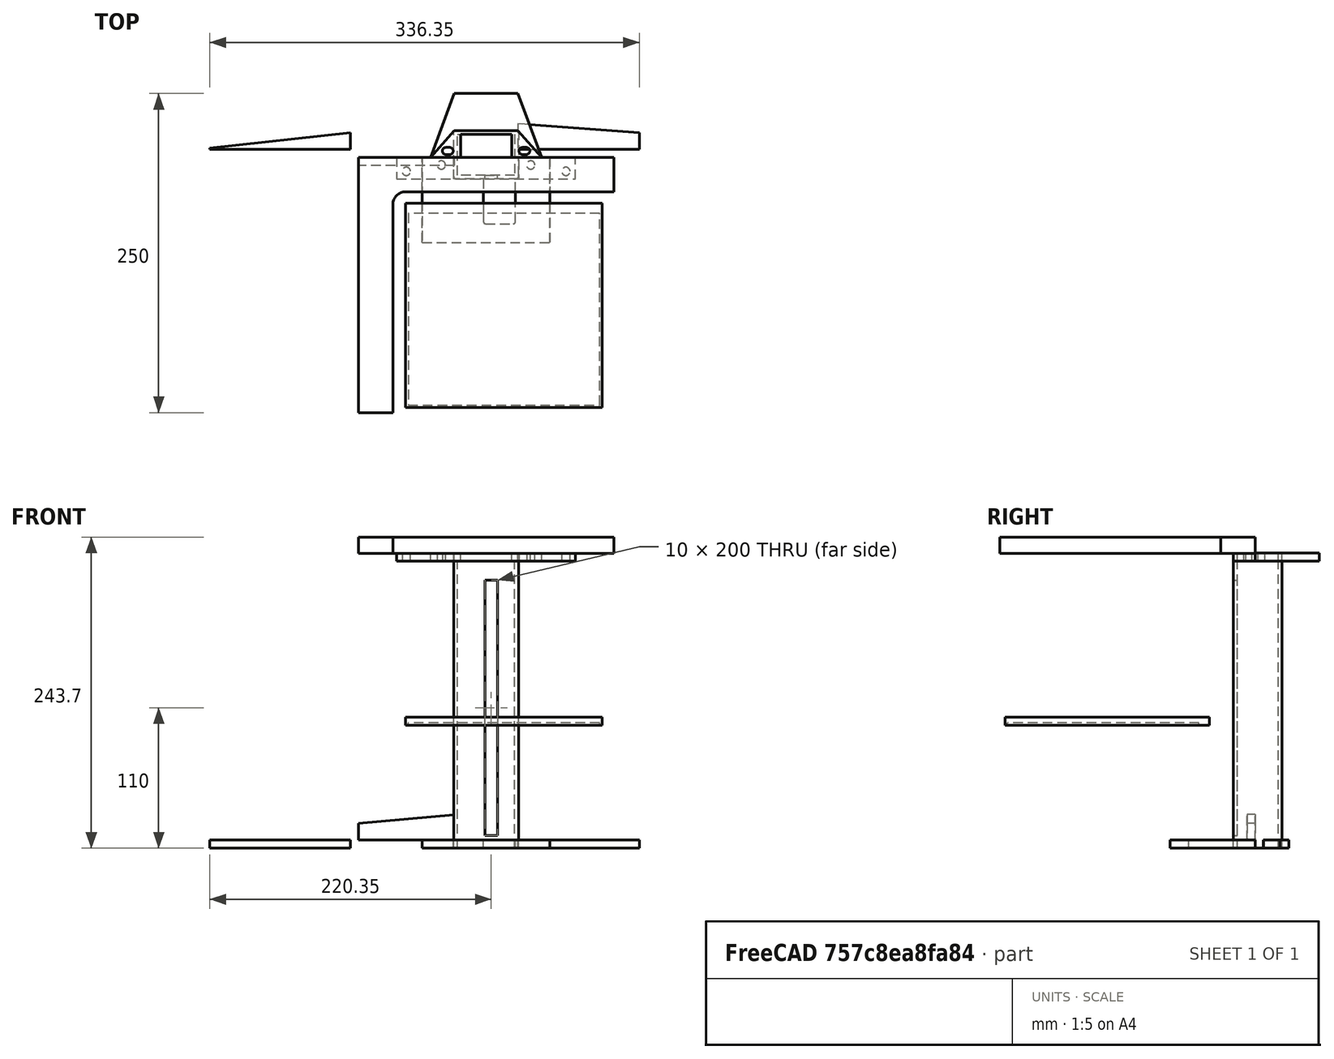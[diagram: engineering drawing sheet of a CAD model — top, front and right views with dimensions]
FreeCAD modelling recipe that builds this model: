
FCSTD DOCUMENT  (FreeCAD 0.19R)
Label: Printer3_tbp
License: All rights reserved
LicenseURL: http://en.wikipedia.org/wiki/All_rights_reserved
objects: Sketcher::SketchObject×18, PartDesign::Pad×9, PartDesign::Body×9, PartDesign::Pocket×4, PartDesign::Fillet×1, Mesh::Feature×1
note: 55 computed .brp shape members not serialized (recipe doc carries the construction recipe); baked Part::Feature solids carry a one-line shape summary decoded from their .brp

FEATURE [Sketcher::SketchObject] Sketch
  FullyConstrained = false
  MapMode = 5
  sketch-geometry (25):
    g0: LineSegment StartX=220 StartY=-2.5 StartZ=0 EndX=220 EndY=-219.878 EndZ=0
    g1: LineSegment StartX=210 StartY=-229.878 StartZ=0 EndX=10 EndY=-229.878 EndZ=0
    g2: LineSegment StartX=0 StartY=-219.878 StartZ=0 EndX=0 EndY=-2.5 EndZ=0
    g3: LineSegment StartX=2.5 StartY=0 StartZ=0 EndX=74.5 EndY=0 EndZ=0
    g4: LineSegment StartX=74.5 StartY=0 StartZ=0 EndX=74.5 EndY=-14.5 EndZ=0
    g5: LineSegment StartX=125.5 StartY=-14.5 StartZ=0 EndX=125.5 EndY=0 EndZ=0
    g6: LineSegment StartX=125.5 StartY=0 StartZ=0 EndX=217.5 EndY=0 EndZ=0
    g7: LineSegment StartX=100 StartY=29.7116 StartZ=0 EndX=100 EndY=-38.9559 EndZ=0
    g8: ArcOfCircle CenterX=2.5 CenterY=-2.5 CenterZ=0 NormalX=0 NormalY=0 NormalZ=1 AngleXU=0 Radius=2.5 StartAngle=1.5708 EndAngle=3.14159
    g9: ArcOfCircle CenterX=217.5 CenterY=-2.5 CenterZ=0 NormalX=0 NormalY=0 NormalZ=1 AngleXU=0 Radius=2.5 StartAngle=4.63e-14 EndAngle=1.5708
    g10: ArcOfCircle CenterX=210 CenterY=-219.878 CenterZ=0 NormalX=0 NormalY=0 NormalZ=1 AngleXU=0 Radius=10 StartAngle=4.71239 EndAngle=6.28319
    g11: ArcOfCircle CenterX=10 CenterY=-219.878 CenterZ=0 NormalX=0 NormalY=0 NormalZ=1 AngleXU=0 Radius=10 StartAngle=3.14159 EndAngle=4.71239
    g12: ArcOfCircle CenterX=123 CenterY=-14.5 CenterZ=0 NormalX=0 NormalY=0 NormalZ=1 AngleXU=0 Radius=2.5 StartAngle=4.71239 EndAngle=6.28319
    g13: ArcOfCircle CenterX=77 CenterY=-14.5 CenterZ=0 NormalX=0 NormalY=0 NormalZ=1 AngleXU=0 Radius=2.5 StartAngle=3.14159 EndAngle=4.71239
    g14: LineSegment StartX=98 StartY=-17 StartZ=0 EndX=98 EndY=-50.5 EndZ=0
    g15: LineSegment StartX=99.5 StartY=-52 StartZ=0 EndX=121.5 EndY=-52 EndZ=0
    g16: LineSegment StartX=123 StartY=-50.5 StartZ=0 EndX=123 EndY=-17 EndZ=0
    g17: LineSegment StartX=77 StartY=-17 StartZ=0 EndX=98 EndY=-17 EndZ=0
    g18: ArcOfCircle CenterX=99.5 CenterY=-50.5 CenterZ=0 NormalX=0 NormalY=0 NormalZ=1 AngleXU=0 Radius=1.5 StartAngle=3.14159 EndAngle=4.71239
    g19: ArcOfCircle CenterX=121.5 CenterY=-50.5 CenterZ=0 NormalX=0 NormalY=0 NormalZ=1 AngleXU=0 Radius=1.5 StartAngle=4.71239 EndAngle=6.28319
    g20: Circle CenterX=207 CenterY=-216.878 CenterZ=0 NormalX=0 NormalY=0 NormalZ=1 AngleXU=0 Radius=2.25
    g21: Circle CenterX=13 CenterY=-216.878 CenterZ=0 NormalX=0 NormalY=0 NormalZ=1 AngleXU=0 Radius=2.25
    g22: Circle CenterX=207 CenterY=-13 CenterZ=0 NormalX=0 NormalY=0 NormalZ=1 AngleXU=0 Radius=2.25
    g23: Circle CenterX=13 CenterY=-13 CenterZ=0 NormalX=0 NormalY=0 NormalZ=1 AngleXU=0 Radius=2.25
    g24: LineSegment StartX=110 StartY=54.384 StartZ=0 EndX=110 EndY=-317.389 EndZ=0
  constraints (63):
    c: Vertical(g0)
    c: Vertical(g2)
    c: Equal(g2,g0)
    c: PointOnObject(g3,g-1)
    c: Horizontal(g3)
    c: Coincident(g3,g4)
    c: PointOnObject(g5,g-1)
    c: Coincident(g5,g6)
    c: Horizontal(g6)
    c: Vertical(g5)
    c: Vertical(g4)
    c: Symmetric(g5,g3,g7)
    c: DistanceX(g7) = 100
    c: Tangent(g2,g8) = 1.5708
    c: Tangent(g3,g8) = 1.5708
    c: Tangent(g6,g9) = 1.5708
    c: Tangent(g0,g9) = 1.5708
    c: Tangent(g1,g10) = 1.5708
    c: Tangent(g0,g10) = 1.5708
    c: Tangent(g1,g11) = 1.5708
    c: Tangent(g2,g11) = 1.5708
    c: PointOnObject(g2,g-2)
    c: Tangent(g5,g12) = -1.5708
    c: Tangent(g4,g13) = -1.5708
    c: Equal(g12,g13)
    c: Distance(g5,g3) = 51
    c: Vertical(g14)
    c: Vertical(g16)
    c: Horizontal(g17)
    c: DistanceY(g12) = -17
    c: Tangent(g14,g18) = -1.5708
    c: Tangent(g15,g18) = -1.5708
    c: Tangent(g16,g19) = -1.5708
    c: Tangent(g15,g19) = -1.5708
    c: DistanceY(g17) = -17
    c: Distance(g16,g14) = 25
    c: Tangent(g17,g13) = -1.5708
    c: DistanceY(g15,g16) = 35
    c: Coincident(g14,g17)
    c: Horizontal(g15)
    c: Diameter(g19) = 3
    c: Diameter(g10) = 20
    c: Diameter(g11) = 20
    c: Diameter(g9) = 5
    c: Diameter(g8) = 5
    c: Distance(g0,g2) = 220
    c: Distance(g6,g1) = 230
    c: Diameter(g18) = 3
    c: Diameter(g13) = 5
    c: Coincident(g16,g12)
    c: Perpendicular(g12,g16)
    c: Diameter(g23) = 4.5
    c: Equal(g23,g22)
    c: Equal(g23,g20)
    c: Diameter(g21) = 4.5
    c: Vertical(g24)
    c: DistanceX(g24) = 110
    c: Symmetric(g22,g23,g24)
    c: Symmetric(g20,g21,g24)
    c: Distance(g20,g0) = 13
    c: Distance(g20,g1) = 13
    c: Distance(g22,g0) = 13
    c: Distance(g22,g6) = 13
FEATURE [PartDesign::Pad] Pad
  Direction = (1,1,1)
  Length = 6.35
  Length2 = 100
  Profile = -> Sketch
  Type = 0
FEATURE [Sketcher::SketchObject] Sketch006
  FullyConstrained = false
  MapMode = 5
  Support = -> [XY_Plane002]
  sketch-geometry (9):
    g0: LineSegment StartX=74.6 StartY=21 StartZ=0 EndX=125.4 EndY=21 EndZ=0
    g1: LineSegment StartX=125.4 StartY=21 StartZ=0 EndX=125.4 EndY=-17 EndZ=0
    g2: LineSegment StartX=125.4 StartY=-17 StartZ=0 EndX=74.6 EndY=-17 EndZ=0
    g3: LineSegment StartX=74.6 StartY=-17 StartZ=0 EndX=74.6 EndY=21 EndZ=0
    g4: LineSegment StartX=100 StartY=34.7898 StartZ=0 EndX=100 EndY=11.1526 EndZ=0
    g5: LineSegment StartX=77.6 StartY=18 StartZ=0 EndX=122.4 EndY=18 EndZ=0
    g6: LineSegment StartX=122.4 StartY=18 StartZ=0 EndX=122.4 EndY=-14 EndZ=0
    g7: LineSegment StartX=122.4 StartY=-14 StartZ=0 EndX=77.6 EndY=-14 EndZ=0
    g8: LineSegment StartX=77.6 StartY=-14 StartZ=0 EndX=77.6 EndY=18 EndZ=0
  constraints (25):
    c: Coincident(g0,g1)
    c: Coincident(g1,g2)
    c: Coincident(g2,g3)
    c: Coincident(g3,g0)
    c: Horizontal(g0)
    c: Horizontal(g2)
    c: Vertical(g1)
    c: Vertical(g3)
    c: Distance(g0) = 50.8
    c: Distance(g1) = 38
    c: DistanceY(g1,g-1) = 17
    c: Symmetric(g0,g0,g4)
    c: DistanceX(g4) = 100
    c: Coincident(g5,g6)
    c: Coincident(g6,g7)
    c: Coincident(g7,g8)
    c: Coincident(g8,g5)
    c: Horizontal(g5)
    c: Horizontal(g7)
    c: Vertical(g6)
    c: Vertical(g8)
    c: Distance(g5,g1) = 3
    c: Distance(g5,g0) = 3
    c: Distance(g7,g3) = 3
    c: Distance(g6,g2) = 3
FEATURE [PartDesign::Pad] Pad001
  Direction = (1,1,1)
  Length = 225
  Length2 = 100
  Profile = -> Sketch006
  Type = 0
FEATURE [Sketcher::SketchObject] Sketch007
  FullyConstrained = true
  MapMode = 5
  Placement = pos=(0,-17,0) rot=(1,0,0;1.5708rad)
  Support = -> [Pad001]
  sketch-geometry (4):
    g0: LineSegment StartX=99 StartY=210 StartZ=0 EndX=109 EndY=210 EndZ=0
    g1: LineSegment StartX=109 StartY=210 StartZ=0 EndX=109 EndY=10 EndZ=0
    g2: LineSegment StartX=109 StartY=10 StartZ=0 EndX=99 EndY=10 EndZ=0
    g3: LineSegment StartX=99 StartY=10 StartZ=0 EndX=99 EndY=210 EndZ=0
  constraints (12):
    c: Coincident(g0,g1)
    c: Coincident(g1,g2)
    c: Coincident(g2,g3)
    c: Coincident(g3,g0)
    c: Horizontal(g0)
    c: Horizontal(g2)
    c: Vertical(g1)
    c: Vertical(g3)
    c: Distance(g2) = 10
    c: DistanceX(g1) = 109
    c: DistanceY(g1) = 10
    c: Distance(g1) = 200
FEATURE [PartDesign::Pocket] Pocket
  BaseFeature = -> Pad001
  Length = 5
  Length2 = 100
  Profile = -> Sketch007
  Type = 0
FEATURE [Sketcher::SketchObject] Sketch009
  FullyConstrained = true
  MapMode = 5
  Placement = pos=(0,0,0) rot=(1,0,0;1.5708rad)
  Support = -> [XZ_Plane004]
  sketch-geometry (4):
    g0: LineSegment StartX=75 StartY=6.35 StartZ=0 EndX=75 EndY=26.35 EndZ=0
    g1: LineSegment StartX=75 StartY=26.35 StartZ=0 EndX=0 EndY=19.35 EndZ=0
    g2: LineSegment StartX=0 StartY=19.35 StartZ=0 EndX=0 EndY=6.35 EndZ=0
    g3: LineSegment StartX=0 StartY=6.35 StartZ=0 EndX=75 EndY=6.35 EndZ=0
  constraints (12):
    c: Vertical(g0)
    c: Coincident(g0,g1)
    c: Coincident(g1,g2)
    c: Coincident(g2,g3)
    c: Coincident(g3,g0)
    c: Horizontal(g3)
    c: Distance(g0) = 20
    c: Vertical(g2)
    c: Distance(g2) = 13
    c: DistanceX(g0) = 75
    c: DistanceY(g2) = 6.35
    c: PointOnObject(g1,g-2)
FEATURE [PartDesign::Pad] Pad003
  Direction = (1,1,1)
  Length = 6.35
  Length2 = 100
  Placement = pos=(0,0,0) rot=(1,0,0;1.5708rad)
  Profile = -> Sketch009
  Type = 0
FEATURE [PartDesign::Body] Body004  label="Gusset1"
  Group = -> [Sketch009,Pad003]
  Origin = -> Origin004
  Placement = pos=(0,-22,0) rot=(0,0,1;0rad)
  Tip = -> Pad003
FEATURE [Sketcher::SketchObject] Sketch010
  FullyConstrained = true
  MapMode = 5
  sketch-geometry (4):
    g0: LineSegment StartX=-6.35 StartY=6.35 StartZ=0 EndX=-6.35 EndY=19.35 EndZ=0
    g1: LineSegment StartX=-6.35 StartY=19.35 StartZ=0 EndX=-116.35 EndY=7.35 EndZ=0
    g2: LineSegment StartX=-116.35 StartY=7.35 StartZ=0 EndX=-116.35 EndY=6.35 EndZ=0
    g3: LineSegment StartX=-116.35 StartY=6.35 StartZ=0 EndX=-6.35 EndY=6.35 EndZ=0
  constraints (12):
    c: Vertical(g0)
    c: Coincident(g0,g1)
    c: Coincident(g1,g2)
    c: Vertical(g2)
    c: Coincident(g2,g3)
    c: Coincident(g3,g0)
    c: Horizontal(g3)
    c: Distance(g2) = 1
    c: Distance(g0) = 13
    c: DistanceY(g0) = 6.35
    c: DistanceX(g0) = -6.35
    c: Distance(g3) = 110
FEATURE [PartDesign::Pad] Pad004
  Direction = (1,1,1)
  Length = 6.35
  Length2 = 100
  Profile = -> Sketch010
  Type = 0
FEATURE [PartDesign::Body] Body005  label="Gusset2"
  Group = -> [Sketch010,Pad004]
  Origin = -> Origin005
  Placement = pos=(0,-22,0) rot=(0,0,1;0rad)
  Tip = -> Pad004
FEATURE [Sketcher::SketchObject] Sketch011
  FullyConstrained = true
  MapMode = 5
  sketch-geometry (4):
    g0: LineSegment StartX=125 StartY=26.35 StartZ=0 EndX=125 EndY=6.35 EndZ=0
    g1: LineSegment StartX=125 StartY=6.35 StartZ=0 EndX=220 EndY=6.35 EndZ=0
    g2: LineSegment StartX=220 StartY=6.35 StartZ=0 EndX=220 EndY=19.35 EndZ=0
    g3: LineSegment StartX=220 StartY=19.35 StartZ=0 EndX=125 EndY=26.35 EndZ=0
  constraints (12):
    c: Vertical(g0)
    c: Coincident(g0,g1)
    c: Horizontal(g1)
    c: Coincident(g1,g2)
    c: Vertical(g2)
    c: Coincident(g2,g3)
    c: Coincident(g3,g0)
    c: Distance(g0) = 20
    c: DistanceY(g0) = 6.35
    c: DistanceX(g0) = 125
    c: DistanceX(g2) = 220
    c: Distance(g2) = 13
FEATURE [PartDesign::Pad] Pad005
  Direction = (1,1,1)
  Length = 6.35
  Length2 = 100
  Profile = -> Sketch011
  Type = 0
FEATURE [PartDesign::Body] Body006  label="Gusset3"
  Group = -> [Sketch011,Pad005]
  Origin = -> Origin006
  Placement = pos=(0,-22,0) rot=(0,0,1;0rad)
  Tip = -> Pad005
FEATURE [Sketcher::SketchObject] Sketch012
  FullyConstrained = false
  MapMode = 5
  Support = -> [XY_Plane007]
  sketch-geometry (5):
    g0: LineSegment StartX=37 StartY=-30 StartZ=0 EndX=191 EndY=-30 EndZ=0
    g1: LineSegment StartX=191 StartY=-30 StartZ=0 EndX=191 EndY=-190 EndZ=0
    g2: LineSegment StartX=191 StartY=-190 StartZ=0 EndX=37 EndY=-190 EndZ=0
    g3: LineSegment StartX=37 StartY=-190 StartZ=0 EndX=37 EndY=-30 EndZ=0
    g4: LineSegment StartX=114 StartY=-22.3792 StartZ=0 EndX=114 EndY=-218.376 EndZ=0
  constraints (13):
    c: Coincident(g0,g1)
    c: Coincident(g1,g2)
    c: Coincident(g2,g3)
    c: Coincident(g3,g0)
    c: Horizontal(g0)
    c: Horizontal(g2)
    c: Vertical(g1)
    c: Vertical(g3)
    c: DistanceX(g0) = 37
    c: DistanceY(g0) = -30
    c: Distance(g2) = 154
    c: Distance(g1) = 160
    c: Symmetric(g0,g0,g4)
FEATURE [PartDesign::Pad] Pad006
  Direction = (1,1,1)
  Length = 6.35
  Length2 = 100
  Profile = -> Sketch012
  Type = 0
FEATURE [Sketcher::SketchObject] Sketch013
  FullyConstrained = true
  MapMode = 5
  Placement = pos=(0,0,0) rot=(1,0,0;3.14159rad)
  Support = -> [Pad006]
  sketch-geometry (4):
    g0: LineSegment StartX=39 StartY=188 StartZ=0 EndX=189 EndY=188 EndZ=0
    g1: LineSegment StartX=189 StartY=188 StartZ=0 EndX=189 EndY=38 EndZ=0
    g2: LineSegment StartX=189 StartY=38 StartZ=0 EndX=39 EndY=38 EndZ=0
    g3: LineSegment StartX=39 StartY=38 StartZ=0 EndX=39 EndY=188 EndZ=0
  constraints (12):
    c: Coincident(g0,g1)
    c: Coincident(g1,g2)
    c: Coincident(g2,g3)
    c: Coincident(g3,g0)
    c: Horizontal(g0)
    c: Horizontal(g2)
    c: Vertical(g1)
    c: Vertical(g3)
    c: Distance(g0) = 150
    c: DistanceY(g0) = 188
    c: Distance(g1) = 150
    c: DistanceX(g0) = 39
FEATURE [PartDesign::Pocket] Pocket001
  BaseFeature = -> Pad006
  Length = 2
  Length2 = 100
  Profile = -> Sketch013
  Type = 0
FEATURE [PartDesign::Body] Body007  label="Bed"
  Group = -> [Sketch012,Pad006,Sketch013,Pocket001]
  Origin = -> Origin007
  Placement = pos=(0,-28,96.35) rot=(0,0,1;0rad)
  Tip = -> Pocket001
FEATURE [Sketcher::SketchObject] Sketch014
  FullyConstrained = true
  MapMode = 5
  Support = -> [XY_Plane008]
  sketch-geometry (4):
    g0: LineSegment StartX=0 StartY=0 StartZ=0 EndX=200 EndY=0 EndZ=0
    g1: LineSegment StartX=200 StartY=0 StartZ=0 EndX=200 EndY=-200 EndZ=0
    g2: LineSegment StartX=200 StartY=-200 StartZ=0 EndX=0 EndY=-200 EndZ=0
    g3: LineSegment StartX=0 StartY=-200 StartZ=0 EndX=0 EndY=0 EndZ=0
  constraints (11):
    c: Coincident(g0,g1)
    c: Coincident(g1,g2)
    c: Coincident(g2,g3)
    c: Coincident(g3,g0)
    c: Horizontal(g0)
    c: Horizontal(g2)
    c: Vertical(g1)
    c: Vertical(g3)
    c: Coincident(g0,g-1)
    c: Distance(g0) = 200
    c: Distance(g1) = 200
FEATURE [PartDesign::Pad] Pad007
  Direction = (1,1,1)
  Length = 12.7
  Length2 = 100
  Profile = -> Sketch014
  Type = 0
FEATURE [Sketcher::SketchObject] Sketch015
  FullyConstrained = false
  MapMode = 5
  Placement = pos=(0,0,12.7) rot=(0,0,1;0rad)
  Support = -> [Pad007]
  sketch-geometry (4):
    g0: LineSegment StartX=27 StartY=-27 StartZ=0 EndX=356.815 EndY=-27 EndZ=0
    g1: LineSegment StartX=356.815 StartY=-27 StartZ=0 EndX=356.815 EndY=-319.156 EndZ=0
    g2: LineSegment StartX=356.815 StartY=-319.156 StartZ=0 EndX=27 EndY=-319.156 EndZ=0
    g3: LineSegment StartX=27 StartY=-319.156 StartZ=0 EndX=27 EndY=-27 EndZ=0
  constraints (10):
    c: Coincident(g0,g1)
    c: Coincident(g1,g2)
    c: Coincident(g2,g3)
    c: Coincident(g3,g0)
    c: Horizontal(g0)
    c: Horizontal(g2)
    c: Vertical(g1)
    c: Vertical(g3)
    c: DistanceX(g0) = 27
    c: DistanceY(g0) = -27
FEATURE [PartDesign::Pocket] Pocket002
  BaseFeature = -> Pad007
  Length = 13
  Length2 = 100
  Profile = -> Sketch015
  Type = 0
FEATURE [PartDesign::Fillet] Fillet
  Base = -> Pocket002 [Edge18]
  BaseFeature = -> Pocket002
  Radius = 10
  SupportTransform = false
FEATURE [Sketcher::SketchObject] Sketch016
  FullyConstrained = false
  MapMode = 5
  Placement = pos=(0,0,0) rot=(1,0,0;3.14159rad)
  Support = -> [Pad]
  sketch-geometry (8):
    g0: LineSegment StartX=150 StartY=11.5558 StartZ=0 EndX=150 EndY=-66.6529 EndZ=0
    g1: LineSegment StartX=150 StartY=-66.6529 StartZ=0 EndX=50 EndY=-66.6529 EndZ=0
    g2: LineSegment StartX=50 StartY=-66.6529 StartZ=0 EndX=50 EndY=26.8046 EndZ=0
    g3: LineSegment StartX=50 StartY=26.8046 StartZ=0 EndX=-42.6332 EndY=26.8046 EndZ=0
    g4: LineSegment StartX=-42.6332 StartY=26.8046 StartZ=0 EndX=-42.6332 EndY=-265.193 EndZ=0
    g5: LineSegment StartX=-42.6332 StartY=-265.193 StartZ=0 EndX=358.07 EndY=-265.193 EndZ=0
    g6: LineSegment StartX=358.07 StartY=-265.193 StartZ=0 EndX=358.07 EndY=30.5784 EndZ=0
    g7: LineSegment StartX=358.07 StartY=30.5784 StartZ=0 EndX=150 EndY=11.5558 EndZ=0
  constraints (17):
    c: Vertical(g0)
    c: Coincident(g0,g1)
    c: Horizontal(g1)
    c: Coincident(g1,g2)
    c: Vertical(g2)
    c: Coincident(g2,g3)
    c: Horizontal(g3)
    c: Coincident(g3,g4)
    c: Vertical(g4)
    c: Coincident(g4,g5)
    c: Horizontal(g5)
    c: Coincident(g5,g6)
    c: Vertical(g6)
    c: Coincident(g6,g7)
    c: Coincident(g7,g0)
    c: DistanceX(g1) = 50
    c: DistanceX(g0) = 150
FEATURE [PartDesign::Pocket] Pocket003
  BaseFeature = -> Pad
  Length = 9
  Length2 = 100
  Profile = -> Sketch016
  Type = 0
FEATURE [Sketcher::SketchObject] Sketch017
  FullyConstrained = false
  MapMode = 5
  Placement = pos=(0,-17,0) rot=(1,0,0;1.5708rad)
  Support = -> [Pocket]
  sketch-geometry (9):
    g0: LineSegment StartX=89 StartY=196.442 StartZ=0 EndX=97 EndY=196.442 EndZ=0
    g1: LineSegment StartX=97 StartY=196.442 StartZ=0 EndX=97 EndY=176.538 EndZ=0
    g2: LineSegment StartX=97 StartY=176.538 StartZ=0 EndX=89 EndY=176.538 EndZ=0
    g3: LineSegment StartX=89 StartY=176.538 StartZ=0 EndX=89 EndY=196.442 EndZ=0
    g4: LineSegment StartX=100 StartY=275.798 StartZ=0 EndX=100 EndY=-189.424 EndZ=0
    g5: LineSegment StartX=93 StartY=214.672 StartZ=0 EndX=93 EndY=194.243 EndZ=0
    g6: LineSegment StartX=123 StartY=219.526 StartZ=0 EndX=123 EndY=197.969 EndZ=0
    g7: LineSegment StartX=102.65 StartY=201.069 StartZ=0 EndX=102.65 EndY=188.207 EndZ=0
    g8: LineSegment StartX=109 StartY=200.806 StartZ=0 EndX=109 EndY=186.098 EndZ=0
  constraints (19):
    c: Coincident(g0,g1)
    c: Coincident(g1,g2)
    c: Coincident(g2,g3)
    c: Coincident(g3,g0)
    c: Horizontal(g0)
    c: Horizontal(g2)
    c: Vertical(g1)
    c: Vertical(g3)
    c: Vertical(g4)
    c: DistanceX(g4) = 100
    c: Distance(g0) = 8
    c: Vertical(g6)
    c: Distance(g6,g4) = 23
    c: Distance(g5,g6) = 30
    c: Symmetric(g0,g0,g5)
    c: Vertical(g7)
    c: Distance(g7,g6) = 20.35
    c: Vertical(g8)
    c: Distance(g8,g7) = 6.35
FEATURE [Sketcher::SketchObject] Sketch018
  FullyConstrained = true
  MapMode = 5
  Placement = pos=(0,0,225) rot=(0,0,1;0rad)
  Support = -> [Pocket]
FEATURE [PartDesign::Body] Body002  label="Column"
  Group = -> [Sketch006,Pad001,Sketch007,Pocket,Sketch017,Sketch018]
  Origin = -> Origin002
  Placement = pos=(0,-22,0) rot=(0,0,1;0rad)
  Tip = -> Pocket
FEATURE [Sketcher::SketchObject] Sketch019
  ExternalGeometry = -> [Pocket003]
  FullyConstrained = true
  MapMode = 5
  Placement = pos=(0,0,6.35) rot=(0,0,1;0rad)
  Support = -> [Pocket003]
FEATURE [Sketcher::SketchObject] Sketch020
  ExternalGeometry = -> [Pad]
  FullyConstrained = false
  MapMode = 5
  Placement = pos=(0,0,0) rot=(1,0,0;3.14159rad)
  Support = -> [Pad]
  sketch-geometry (4):
    g0: LineSegment StartX=92.1821 StartY=-18.4998 StartZ=0 EndX=96.667 EndY=-18.4998 EndZ=0
    g1: LineSegment StartX=96.667 StartY=-18.4998 StartZ=0 EndX=96.667 EndY=-3 EndZ=0
    g2: LineSegment StartX=96.667 StartY=-3 StartZ=0 EndX=92.1821 EndY=-3 EndZ=0
    g3: LineSegment StartX=92.1821 StartY=-3 StartZ=0 EndX=92.1821 EndY=-18.4998 EndZ=0
  constraints (9):
    c: Coincident(g0,g1)
    c: Coincident(g1,g2)
    c: Coincident(g2,g3)
    c: Coincident(g3,g0)
    c: Horizontal(g0)
    c: Horizontal(g2)
    c: Vertical(g1)
    c: Vertical(g3)
    c: Distance(g1,g-3) = 20
FEATURE [PartDesign::Body] Body  label="Base"
  Group = -> [Sketch,Pad,Sketch016,Pocket003,Sketch019,Sketch020]
  Origin = -> Origin
  Placement = pos=(0,-22,0) rot=(0,0,1;0rad)
  Tip = -> Pocket003
FEATURE [Sketcher::SketchObject] Sketch021
  FullyConstrained = false
  MapMode = 5
  Placement = pos=(0,0,12.7) rot=(0,0,1;0rad)
  Support = -> [Fillet]
  sketch-geometry (3):
    g0: Circle CenterX=5 CenterY=-5 CenterZ=0 NormalX=0 NormalY=0 NormalZ=1 AngleXU=0 Radius=3.84809
    g1: LineSegment StartX=100 StartY=-3.69453 StartZ=0 EndX=100 EndY=-13.0067 EndZ=0
    g2: LineSegment StartX=26 StartY=35.8308 StartZ=0 EndX=26 EndY=-39.0103 EndZ=0
  constraints (6):
    c: DistanceX(g0) = 5
    c: DistanceY(g0) = -5
    c: Vertical(g1)
    c: DistanceX(g1) = 100
    c: Vertical(g2)
    c: Distance(g0,g2) = 21
FEATURE [PartDesign::Body] Body008  label="gantry"
  Group = -> [Sketch014,Pad007,Sketch015,Pocket002,Fillet,Sketch021]
  Origin = -> Origin008
  Placement = pos=(0,-22,231) rot=(0,0,1;0rad)
  Tip = -> Fillet
FEATURE [Sketcher::SketchObject] Sketch022
  FullyConstrained = false
  MapMode = 5
  sketch-geometry (25):
    g0: LineSegment StartX=30 StartY=-17 StartZ=0 EndX=170 EndY=-17 EndZ=0
    g1: LineSegment StartX=170 StartY=-17 StartZ=0 EndX=170 EndY=0 EndZ=0
    g2: LineSegment StartX=170 StartY=0 StartZ=0 EndX=143.52 EndY=0 EndZ=0
    g3: LineSegment StartX=143.52 StartY=0 StartZ=0 EndX=125 EndY=21 EndZ=0
    g4: LineSegment StartX=125 StartY=21 StartZ=0 EndX=75 EndY=21 EndZ=0
    g5: LineSegment StartX=75 StartY=21 StartZ=0 EndX=56.4797 EndY=0 EndZ=0
    g6: LineSegment StartX=56.4797 StartY=0 StartZ=0 EndX=30 EndY=0 EndZ=0
    g7: LineSegment StartX=30 StartY=0 StartZ=0 EndX=30 EndY=-17 EndZ=0
    g8: LineSegment StartX=100 StartY=41.9459 StartZ=0 EndX=100 EndY=-57.4771 EndZ=0
    g9: ArcOfCircle CenterX=68.5 CenterY=5 CenterZ=0 NormalX=0 NormalY=0 NormalZ=1 AngleXU=0 Radius=2.75 StartAngle=1.5708 EndAngle=4.71239
    g10: ArcOfCircle CenterX=71.5 CenterY=5 CenterZ=0 NormalX=0 NormalY=0 NormalZ=1 AngleXU=0 Radius=2.75 StartAngle=4.71239 EndAngle=7.85398
    g11: LineSegment StartX=68.5 StartY=2.25 StartZ=0 EndX=71.5 EndY=2.25 EndZ=0
    g12: LineSegment StartX=68.5 StartY=7.75 StartZ=0 EndX=71.5 EndY=7.75 EndZ=0
    g13: ArcOfCircle CenterX=128.5 CenterY=5 CenterZ=0 NormalX=0 NormalY=0 NormalZ=1 AngleXU=0 Radius=2.75 StartAngle=1.5708 EndAngle=4.71239
    g14: ArcOfCircle CenterX=131.5 CenterY=5 CenterZ=0 NormalX=0 NormalY=0 NormalZ=1 AngleXU=0 Radius=2.75 StartAngle=4.71239 EndAngle=7.85398
    g15: LineSegment StartX=128.5 StartY=2.25 StartZ=0 EndX=131.5 EndY=2.25 EndZ=0
    g16: LineSegment StartX=128.5 StartY=7.75 StartZ=0 EndX=131.5 EndY=7.75 EndZ=0
    g17: Circle CenterX=37.5 CenterY=-11 CenterZ=0 NormalX=0 NormalY=0 NormalZ=1 AngleXU=0 Radius=3.25
    g18: Circle CenterX=65 CenterY=-6 CenterZ=0 NormalX=0 NormalY=0 NormalZ=1 AngleXU=0 Radius=3.25
    g19: Circle CenterX=135 CenterY=-6 CenterZ=0 NormalX=0 NormalY=0 NormalZ=1 AngleXU=0 Radius=3.25
    g20: Circle CenterX=162.5 CenterY=-11 CenterZ=0 NormalX=0 NormalY=0 NormalZ=1 AngleXU=0 Radius=3.25
    g21: LineSegment StartX=80 StartY=18 StartZ=0 EndX=120 EndY=18 EndZ=0
    g22: LineSegment StartX=120 StartY=18 StartZ=0 EndX=120 EndY=0 EndZ=0
    g23: LineSegment StartX=120 StartY=0 StartZ=0 EndX=80 EndY=0 EndZ=0
    g24: LineSegment StartX=80 StartY=0 StartZ=0 EndX=80 EndY=18 EndZ=0
  constraints (64):
    c: Horizontal(g0)
    c: Coincident(g0,g1)
    c: PointOnObject(g1,g-1)
    c: Vertical(g1)
    c: Coincident(g1,g2)
    c: PointOnObject(g2,g-1)
    c: Coincident(g2,g3)
    c: Coincident(g3,g4)
    c: Horizontal(g4)
    c: Coincident(g4,g5)
    c: Coincident(g5,g6)
    c: PointOnObject(g6,g-1)
    c: Coincident(g6,g7)
    c: Coincident(g0,g7)
    c: Distance(g1) = 17
    c: Vertical(g7)
    c: DistanceX(g8) = 100
    c: Symmetric(g3,g4,g8)
    c: Symmetric(g2,g5,g8)
    c: Equal(g2,g6)
    c: DistanceY(g3) = 21
    c: Distance(g4) = 50
    c: DistanceX(g0) = 30
    c: Distance(g3) = 28
    c: Tangent(g9,g12) = 1.5708
    c: Tangent(g9,g11) = -1.5708
    c: Tangent(g11,g10) = -1.5708
    c: Tangent(g12,g10) = 1.5708
    c: Horizontal(g11)
    c: Equal(g9,g10)
    c: Tangent(g13,g16) = 1.5708
    c: Tangent(g13,g15) = -1.5708
    c: Tangent(g15,g14) = -1.5708
    c: Tangent(g16,g14) = 1.5708
    c: Horizontal(g15)
    c: Equal(g13,g14)
    c: Diameter(g19) = 6.5
    c: Equal(g19,g18)
    c: Equal(g19,g17)
    c: Symmetric(g18,g19,g8)
    c: Symmetric(g20,g17,g8)
    c: DistanceY(g17) = -11
    c: DistanceY(g18) = -6
    c: Diameter(g20) = 6.5
    c: DistanceX(g20) = 162.5
    c: Distance(g10,g10) = 5.5
    c: Distance(g12) = 3
    c: Distance(g16) = 3
    c: Distance(g13,g13) = 5.5
    c: Symmetric(g14,g9,g8)
    c: DistanceY(g10) = 5
    c: Distance(g14,g10) = 60
    c: Distance(g19,g18) = 70
    c: Coincident(g21,g22)
    c: Coincident(g22,g23)
    c: Coincident(g23,g24)
    c: Coincident(g24,g21)
    c: Horizontal(g21)
    c: Vertical(g22)
    c: Vertical(g24)
    c: Symmetric(g22,g23,g8)
    c: DistanceY(g21) = 18
    c: PointOnObject(g22,g-1)
    c: Distance(g21) = 40
FEATURE [PartDesign::Pad] Pad008
  Direction = (1,1,1)
  Length = 6.35
  Length2 = 100
  Profile = -> Sketch022
  Type = 0
FEATURE [PartDesign::Body] Body009  label="TopPlate"
  Group = -> [Sketch022,Pad008]
  Origin = -> Origin009
  Placement = pos=(0,-22,225) rot=(0,0,1;0rad)
  Tip = -> Pad008
FEATURE [Sketcher::SketchObject] Sketch023
  FullyConstrained = false
  MapMode = 5
  sketch-geometry (21):
    g0: LineSegment StartX=30 StartY=-17 StartZ=0 EndX=170 EndY=-17 EndZ=0
    g1: LineSegment StartX=170 StartY=-17 StartZ=0 EndX=170 EndY=0 EndZ=0
    g2: LineSegment StartX=170 StartY=0 StartZ=0 EndX=143.52 EndY=0 EndZ=0
    g3: LineSegment StartX=143.52 StartY=0 StartZ=0 EndX=125 EndY=50 EndZ=0
    g4: LineSegment StartX=125 StartY=50 StartZ=0 EndX=75 EndY=50 EndZ=0
    g5: LineSegment StartX=75 StartY=50 StartZ=0 EndX=56.48 EndY=0 EndZ=0
    g6: LineSegment StartX=56.48 StartY=0 StartZ=0 EndX=30 EndY=0 EndZ=0
    g7: LineSegment StartX=30 StartY=0 StartZ=0 EndX=30 EndY=-17 EndZ=0
    g8: LineSegment StartX=100 StartY=41.9459 StartZ=0 EndX=100 EndY=-57.4771 EndZ=0
    g9: ArcOfCircle CenterX=68.5 CenterY=5 CenterZ=0 NormalX=0 NormalY=0 NormalZ=1 AngleXU=0 Radius=2.75 StartAngle=1.5708 EndAngle=4.71239
    g10: ArcOfCircle CenterX=71.5 CenterY=5 CenterZ=0 NormalX=0 NormalY=0 NormalZ=1 AngleXU=0 Radius=2.75 StartAngle=4.71239 EndAngle=7.85398
    g11: LineSegment StartX=68.5 StartY=2.25 StartZ=0 EndX=71.5 EndY=2.25 EndZ=0
    g12: LineSegment StartX=68.5 StartY=7.75 StartZ=0 EndX=71.5 EndY=7.75 EndZ=0
    g13: ArcOfCircle CenterX=128.5 CenterY=5 CenterZ=0 NormalX=0 NormalY=0 NormalZ=1 AngleXU=0 Radius=2.75 StartAngle=1.5708 EndAngle=4.71239
    g14: ArcOfCircle CenterX=131.5 CenterY=5 CenterZ=0 NormalX=0 NormalY=0 NormalZ=1 AngleXU=0 Radius=2.75 StartAngle=4.71239 EndAngle=7.85398
    g15: LineSegment StartX=128.5 StartY=2.25 StartZ=0 EndX=131.5 EndY=2.25 EndZ=0
    g16: LineSegment StartX=128.5 StartY=7.75 StartZ=0 EndX=131.5 EndY=7.75 EndZ=0
    g17: Circle CenterX=37.5 CenterY=-11 CenterZ=0 NormalX=0 NormalY=0 NormalZ=1 AngleXU=0 Radius=3.25
    g18: Circle CenterX=65 CenterY=-6 CenterZ=0 NormalX=0 NormalY=0 NormalZ=1 AngleXU=0 Radius=3.25
    g19: Circle CenterX=135 CenterY=-6 CenterZ=0 NormalX=0 NormalY=0 NormalZ=1 AngleXU=0 Radius=3.25
    g20: Circle CenterX=162.5 CenterY=-11 CenterZ=0 NormalX=0 NormalY=0 NormalZ=1 AngleXU=0 Radius=3.25
  constraints (53):
    c: Horizontal(g0)
    c: Coincident(g0,g1)
    c: PointOnObject(g1,g-1)
    c: Vertical(g1)
    c: Coincident(g1,g2)
    c: PointOnObject(g2,g-1)
    c: Coincident(g2,g3)
    c: Coincident(g3,g4)
    c: Horizontal(g4)
    c: Coincident(g4,g5)
    c: Coincident(g5,g6)
    c: PointOnObject(g6,g-1)
    c: Coincident(g6,g7)
    c: Coincident(g0,g7)
    c: Distance(g1) = 17
    c: Vertical(g7)
    c: DistanceX(g8) = 100
    c: Symmetric(g3,g4,g8)
    c: Symmetric(g2,g5,g8)
    c: Equal(g2,g6)
    c: DistanceY(g3) = 50
    c: Distance(g4) = 50
    c: DistanceX(g0) = 30
    c: Tangent(g9,g12) = 1.5708
    c: Tangent(g9,g11) = -1.5708
    c: Tangent(g11,g10) = -1.5708
    c: Tangent(g12,g10) = 1.5708
    c: Horizontal(g11)
    c: Equal(g9,g10)
    c: Tangent(g13,g16) = 1.5708
    c: Tangent(g13,g15) = -1.5708
    c: Tangent(g15,g14) = -1.5708
    c: Tangent(g16,g14) = 1.5708
    c: Horizontal(g15)
    c: Equal(g13,g14)
    c: Diameter(g19) = 6.5
    c: Equal(g19,g18)
    c: Equal(g19,g17)
    c: Symmetric(g18,g19,g8)
    c: Symmetric(g20,g17,g8)
    c: DistanceY(g17) = -11
    c: DistanceY(g18) = -6
    c: Diameter(g20) = 6.5
    c: DistanceX(g20) = 162.5
    c: Distance(g10,g10) = 5.5
    c: Distance(g12) = 3
    c: Distance(g16) = 3
    c: Distance(g13,g13) = 5.5
    c: Symmetric(g14,g9,g8)
    c: DistanceY(g10) = 5
    c: Distance(g14,g10) = 60
    c: Distance(g19,g18) = 70
    c: Distance(g2) = 26.48
FEATURE [PartDesign::Pad] Pad009
  Direction = (1,1,1)
  Length = 6.35
  Length2 = 100
  Profile = -> Sketch023
  Type = 0
FEATURE [PartDesign::Body] Body010  label="Fixture"
  Group = -> [Sketch023,Pad009]
  Origin = -> Origin010
  Placement = pos=(0,-22,225) rot=(0,0,1;0rad)
  Tip = -> Pad009
FEATURE [Mesh::Feature] Mesh  label="Pad009 (Meshed)"
